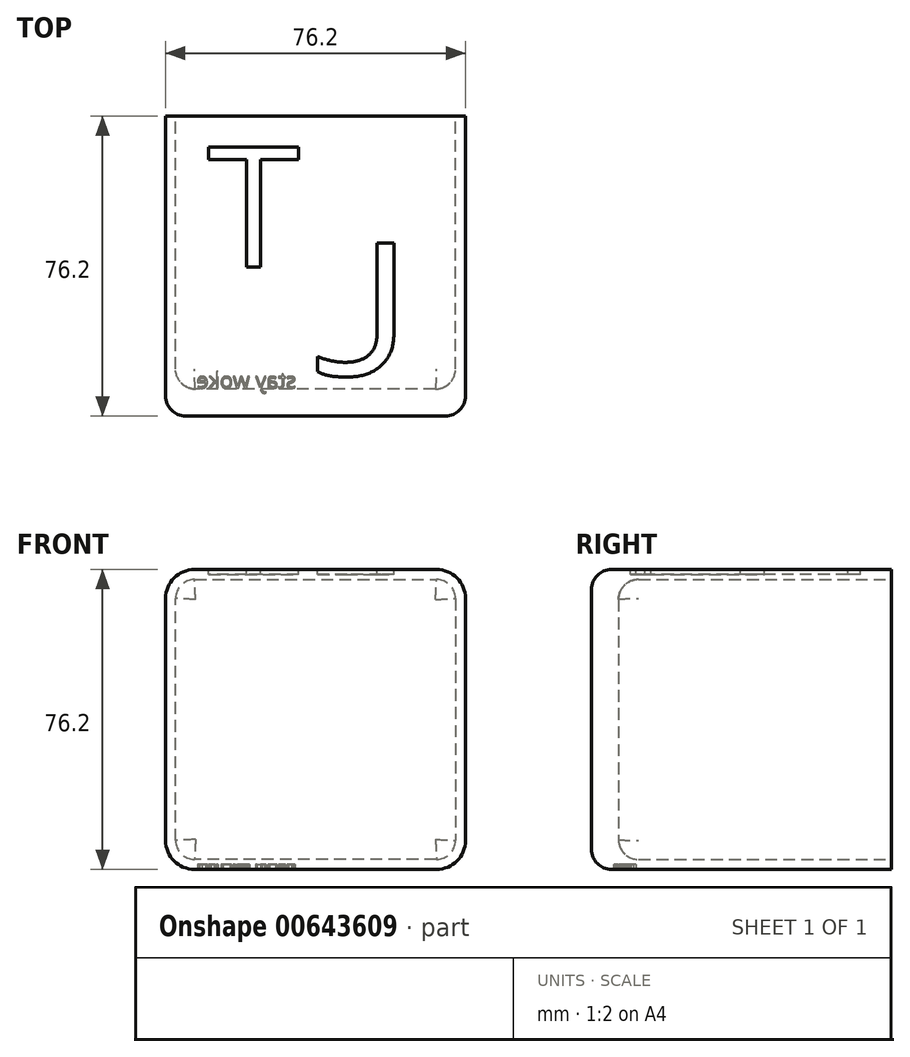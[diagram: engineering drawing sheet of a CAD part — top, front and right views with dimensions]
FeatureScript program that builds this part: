
annotation { "Feature Type Name" : "Feature", "Feature Type Description" : "" }
export const myFeature = defineFeature(function(context is Context, id is Id, definition is map)
    precondition{}
    {
        {
            var Q0;
            Q0=qCreatedBy(makeId("Front.planeOp"),FACE);
            var sketch = newSketch(context, id + "F0", { "sketchPlane" : qUnion([Q0])});
            skLineSegment(sketch, "E0.bottom", {"start": v(38.1, 38.1) * mm, "end": v(-38.1, 38.1) * mm});
            skLineSegment(sketch, "E0.top", {"start": v(38.1, -38.1) * mm, "end": v(-38.1, -38.1) * mm});
            skLineSegment(sketch, "E0.left", {"start": v(38.1, 38.1) * mm, "end": v(38.1, -38.1) * mm});
            skLineSegment(sketch, "E0.right", {"start": v(-38.1, 38.1) * mm, "end": v(-38.1, -38.1) * mm});
            skPoint(sketch, "E0.middle", {"position": v(0, 0) * mm});
            skSolve(sketch);
        }
        {
            var Q0;
            Q0=makeQuery(id+"F0.imprint","IMPRINT",FACE,{"disambiguationData":[TD([[makeQuery(id+"F0.imprint","IMPRINT",EDGE,{"derivedFrom":sQuery(id+"F0.wireOp",EDGE,"E0.bottom")}),1.0]])]});
            extrude(context, id + "F1", {"entities" : qUnion([Q0]), "oppositeDirection" : true, "depth" : 76.2 * mm, "offsetDistance" : 25.4 * mm});
        }
        {
            var Q0;
            Q0=makeQuery(id+"F1.opExtrude","SWEPT_EDGE",EDGE,{"disambiguationData":[OSD([sQuery(id+"F0.wireOp",EDGE,"E0.bottom"),sQuery(id+"F0.wireOp",EDGE,"E0.left")])]});
            var Q1;
            Q1=makeQuery(id+"F1.opExtrude","SWEPT_EDGE",EDGE,{"disambiguationData":[OSD([sQuery(id+"F0.wireOp",EDGE,"E0.top"),sQuery(id+"F0.wireOp",EDGE,"E0.left")])]});
            var Q2;
            Q2=makeQuery(id+"F1.opExtrude","SWEPT_EDGE",EDGE,{"disambiguationData":[OSD([sQuery(id+"F0.wireOp",EDGE,"E0.top"),sQuery(id+"F0.wireOp",EDGE,"E0.right")])]});
            var Q3;
            Q3=makeQuery(id+"F1.opExtrude","SWEPT_EDGE",EDGE,{"disambiguationData":[OSD([sQuery(id+"F0.wireOp",EDGE,"E0.bottom"),sQuery(id+"F0.wireOp",EDGE,"E0.right")])]});
            fillet(context, id + "F2", {"entities" : qUnion([Q0, Q1, Q2, Q3]), "radius" : 7.36 * mm, "tangentPropagation" : true, "allowEdgeOverflow" : false});
        }
        {
            var Q0;
            Q0=makeQuery(id+"F1.opExtrude","CAP_FACE",FACE,{"disambiguationData":[OSD([sQuery(id+"F0.wireOp",EDGE,"E0.bottom"),sQuery(id+"F0.wireOp",EDGE,"E0.top"),sQuery(id+"F0.wireOp",EDGE,"E0.left"),sQuery(id+"F0.wireOp",EDGE,"E0.right")])],"isStart":false});
            var sketch = newSketch(context, id + "F3", { "sketchPlane" : qUnion([Q0])});
            skArc(sketch, "E1.0", {"start": v(-30.74, 35.56) * mm, "mid": v(-34.15, 34.15) * mm, "end": v(-35.56, 30.74) * mm});
            skLineSegment(sketch, "E1.1", {"start": v(30.74, 35.56) * mm, "end": v(-30.74, 35.56) * mm});
            skLineSegment(sketch, "E1.2", {"start": v(-35.56, 30.74) * mm, "end": v(-35.56, -30.74) * mm});
            skArc(sketch, "E1.3", {"start": v(35.56, 30.74) * mm, "mid": v(34.15, 34.15) * mm, "end": v(30.74, 35.56) * mm});
            skArc(sketch, "E1.4", {"start": v(-35.56, -30.74) * mm, "mid": v(-34.15, -34.15) * mm, "end": v(-30.74, -35.56) * mm});
            skLineSegment(sketch, "E1.5", {"start": v(-30.74, -35.56) * mm, "end": v(30.74, -35.56) * mm});
            skArc(sketch, "E1.6", {"start": v(30.74, -35.56) * mm, "mid": v(34.15, -34.15) * mm, "end": v(35.56, -30.74) * mm});
            skLineSegment(sketch, "E1.7", {"start": v(35.56, -30.74) * mm, "end": v(35.56, 30.74) * mm});
            skSolve(sketch);
        }
        {
            var Q0;
            Q0=makeQuery(id+"F3.imprint","IMPRINT",FACE,{"disambiguationData":[TD([[makeQuery(id+"F3.imprint","IMPRINT",EDGE,{"derivedFrom":sQuery(id+"F3.wireOp",EDGE,"E1.0")}),1.0]])]});
            extrude(context, id + "F4", {"entities" : qUnion([Q0]), "operationType" : NewBodyOperationType.REMOVE, "oppositeDirection" : true, "depth" : 69.34 * mm, "offsetDistance" : 25.4 * mm});
        }
        {
            var Q0;
            Q0=makeQuery(id+"F1.opExtrude","SWEPT_FACE",FACE,{"disambiguationData":[OSD([sQuery(id+"F0.wireOp",EDGE,"E0.bottom")])]});
            var sketch = newSketch(context, id + "F5", { "sketchPlane" : qUnion([Q0])});
            skPoint(sketch, "E2", {"position": v(-0.05, 16.82) * mm});
            skLineSegment(sketch, "E3", {"start": v(-13.36, 51.7) * mm, "end": v(-8.8, 59.66) * mm});
            skLineSegment(sketch, "E4", {"start": v(-8.8, 59.66) * mm, "end": v(-8.8, 60.27) * mm});
            skLineSegment(sketch, "E5", {"start": v(-8.8, 60.27) * mm, "end": v(8.61, 60.27) * mm});
            skLineSegment(sketch, "E6", {"start": v(8.61, 60.27) * mm, "end": v(8.61, 59.66) * mm});
            skLineSegment(sketch, "E7", {"start": v(8.61, 59.66) * mm, "end": v(13.21, 51.72) * mm});
            skLineSegment(sketch, "E8", {"start": v(13.21, 51.72) * mm, "end": v(12.2, 51.13) * mm});
            skLineSegment(sketch, "E9", {"start": v(12.2, 51.13) * mm, "end": v(18.2, 40.75) * mm});
            skLineSegment(sketch, "E10", {"start": v(18.2, 40.75) * mm, "end": v(19.17, 41.3) * mm});
            skLineSegment(sketch, "E11", {"start": v(19.17, 41.3) * mm, "end": v(23.84, 33.25) * mm});
            skLineSegment(sketch, "E12", {"start": v(23.84, 33.25) * mm, "end": v(24.72, 32.8) * mm});
            skLineSegment(sketch, "E13", {"start": v(24.72, 32.8) * mm, "end": v(16.03, 17.66) * mm});
            skLineSegment(sketch, "E14", {"start": v(16.03, 17.66) * mm, "end": v(15.1, 18.19) * mm});
            skLineSegment(sketch, "E15", {"start": v(15.1, 18.19) * mm, "end": v(5.88, 18.19) * mm});
            skLineSegment(sketch, "E16", {"start": v(5.88, 18.19) * mm, "end": v(5.88, 19.3) * mm});
            skLineSegment(sketch, "E17", {"start": v(5.88, 19.3) * mm, "end": v(-6.04, 19.3) * mm});
            skLineSegment(sketch, "E18", {"start": v(-6.04, 19.3) * mm, "end": v(-6.04, 18.19) * mm});
            skLineSegment(sketch, "E19", {"start": v(-6.04, 18.19) * mm, "end": v(-15.11, 18.19) * mm});
            skLineSegment(sketch, "E20", {"start": v(-15.11, 18.19) * mm, "end": v(-16.13, 17.59) * mm});
            skLineSegment(sketch, "E21", {"start": v(-16.13, 17.59) * mm, "end": v(-24.9, 32.74) * mm});
            skLineSegment(sketch, "E22", {"start": v(-24.9, 32.74) * mm, "end": v(-24.02, 33.24) * mm});
            skLineSegment(sketch, "E23", {"start": v(-24.02, 33.24) * mm, "end": v(-19.39, 41.3) * mm});
            skLineSegment(sketch, "E24", {"start": v(-19.39, 41.3) * mm, "end": v(-18.36, 40.72) * mm});
            skLineSegment(sketch, "E25", {"start": v(-18.36, 40.72) * mm, "end": v(-12.4, 51.1) * mm});
            skLineSegment(sketch, "E26", {"start": v(-12.4, 51.1) * mm, "end": v(-13.36, 51.7) * mm});
            skLineSegment(sketch, "E27", {"start": v(-6.54, 51) * mm, "end": v(6.41, 51) * mm});
            skLineSegment(sketch, "E28", {"start": v(6.41, 51) * mm, "end": v(7.86, 48.5) * mm});
            skLineSegment(sketch, "E29", {"start": v(7.86, 48.5) * mm, "end": v(8.95, 49.12) * mm});
            skLineSegment(sketch, "E30", {"start": v(8.95, 49.12) * mm, "end": v(14.92, 38.82) * mm});
            skLineSegment(sketch, "E31", {"start": v(14.92, 38.82) * mm, "end": v(13.8, 38.17) * mm});
            skLineSegment(sketch, "E32", {"start": v(13.8, 38.17) * mm, "end": v(15.26, 35.63) * mm});
            skLineSegment(sketch, "E33", {"start": v(15.26, 35.63) * mm, "end": v(8.82, 24.4) * mm});
            skLineSegment(sketch, "E34", {"start": v(8.82, 24.4) * mm, "end": v(5.88, 24.4) * mm});
            skLineSegment(sketch, "E35", {"start": v(5.88, 24.4) * mm, "end": v(5.88, 23.2) * mm});
            skLineSegment(sketch, "E36", {"start": v(5.88, 23.2) * mm, "end": v(-5.99, 23.2) * mm});
            skLineSegment(sketch, "E37", {"start": v(-5.99, 23.2) * mm, "end": v(-5.99, 24.36) * mm});
            skLineSegment(sketch, "E38", {"start": v(-5.99, 24.36) * mm, "end": v(-8.88, 24.36) * mm});
            skLineSegment(sketch, "E39", {"start": v(-8.88, 24.36) * mm, "end": v(-15.39, 35.6) * mm});
            skLineSegment(sketch, "E40", {"start": v(-15.39, 35.6) * mm, "end": v(-13.92, 38.15) * mm});
            skLineSegment(sketch, "E41", {"start": v(-13.92, 38.15) * mm, "end": v(-15, 38.76) * mm});
            skLineSegment(sketch, "E42", {"start": v(-15, 38.76) * mm, "end": v(-9.05, 49.11) * mm});
            skLineSegment(sketch, "E43", {"start": v(-9.05, 49.11) * mm, "end": v(-8.01, 48.51) * mm});
            skLineSegment(sketch, "E44", {"start": v(-8.01, 48.51) * mm, "end": v(-6.54, 51) * mm});
            skLineSegment(sketch, "E45.0", {"start": v(30.74, 0) * mm, "end": v(30.74, 76.2) * mm});
            skSolve(sketch);
        }
        {
            var Q0;
            Q0=makeQuery(id+"F4.boolean.opBoolean","COPY",EDGE,{"derivedFrom":makeQuery(id+"F4.opExtrude","CAP_EDGE",EDGE,{"disambiguationData":[OSD([sQuery(id+"F3.wireOp",EDGE,"E1.6")])],"isStart":false})});
            fillet(context, id + "F6", {"entities" : qUnion([Q0]), "radius" : 5.08 * mm, "tangentPropagation" : true, "allowEdgeOverflow" : false});
        }
        {
            var Q0;
            Q0=makeQuery(id+"F1.opExtrude","CAP_FACE",FACE,{"disambiguationData":[OSD([sQuery(id+"F0.wireOp",EDGE,"E0.bottom"),sQuery(id+"F0.wireOp",EDGE,"E0.top"),sQuery(id+"F0.wireOp",EDGE,"E0.left"),sQuery(id+"F0.wireOp",EDGE,"E0.right")])],"isStart":true});
            fillet(context, id + "F7", {"entities" : qUnion([Q0]), "radius" : 5.08 * mm, "tangentPropagation" : true, "allowEdgeOverflow" : false});
        }
        {
            var Q0;
            Q0=makeQuery(id+"F1.opExtrude","SWEPT_FACE",FACE,{"disambiguationData":[OSD([sQuery(id+"F0.wireOp",EDGE,"E0.bottom")])]});
            var sketch = newSketch(context, id + "F8", { "sketchPlane" : qUnion([Q0])});
            skText(sketch, "E46", { "text": "T", "fontName": "OpenSans-Regular.ttf"});
            skText(sketch, "E47", { "text": "J", "fontName": "DroidSansMono.ttf"});
            const initialGuessF8  = {"E46": [-0.0275, 0.0378, 1, 0, 0.03074], "E47": [-0.00262, 0.01035, 1, 0, 0.0339]};
            skSetInitialGuess(sketch, initialGuessF8);
            skSolve(sketch);
        }
        {
            var Q0;
            Q0=makeQuery(id+"F8.imprint","IMPRINT",FACE,{"disambiguationData":[TD([[makeQuery(id+"F8.imprint","IMPRINT",EDGE,{"derivedFrom":sQuery(id+"F8.wireOp",EDGE,"E47.sketch_text.stroke-0")}),-1.0]])]});
            var Q1;
            Q1=makeQuery(id+"F8.imprint","IMPRINT",FACE,{"disambiguationData":[TD([[makeQuery(id+"F8.imprint","IMPRINT",EDGE,{"derivedFrom":sQuery(id+"F8.wireOp",EDGE,"E46.sketch_text.stroke-0")}),-1.0]])]});
            extrude(context, id + "F9", {"entities" : qUnion([Q0, Q1]), "operationType" : NewBodyOperationType.REMOVE, "oppositeDirection" : true, "depth" : 1.27 * mm, "offsetDistance" : 25.4 * mm});
        }
        {
            var Q0;
            Q0=makeQuery(id+"F1.opExtrude","SWEPT_FACE",FACE,{"disambiguationData":[OSD([sQuery(id+"F0.wireOp",EDGE,"E0.top")])]});
            var sketch = newSketch(context, id + "F10", { "sketchPlane" : qUnion([Q0])});
            skText(sketch, "E48", { "text": "stay woke", "fontName": "OpenSans-Regular.ttf"});
            const initialGuessF10  = {"E48": [-0.00492, -0.00709, -1, 0, 0.00395]};
            skSetInitialGuess(sketch, initialGuessF10);
            skSolve(sketch);
        }
        {
            var Q0;
            Q0 = qSketchRegion(id + "F10", true);
            extrude(context, id + "F11", {"entities" : qUnion([Q0]), "operationType" : NewBodyOperationType.REMOVE, "oppositeDirection" : true, "depth" : 1.27 * mm, "offsetDistance" : 25.4 * mm});
        }
    });
